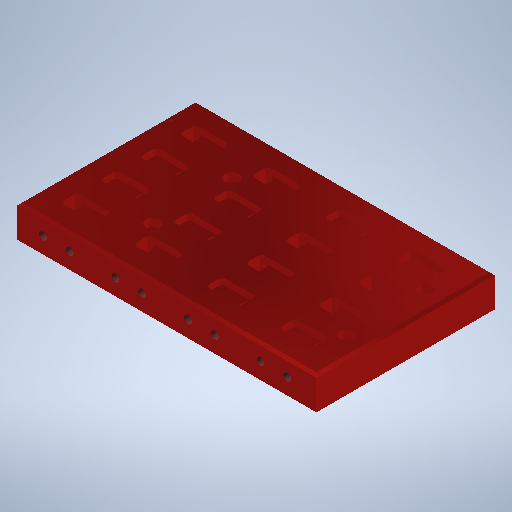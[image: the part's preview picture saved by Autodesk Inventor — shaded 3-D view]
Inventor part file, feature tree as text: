
AUTODESK INVENTOR PART (.ipt)
format: ipt  version: 2025 (Build 290162000, 162)  size: 1,054,208 bytes
history: native  units: mm
features: projected_geometry x17, sketch x9, hole x6, extrude x4, other x2, chamfer x1
ambient origin geometry x8: Origin, YZ Plane, XZ Plane, XY Plane, X Axis, Y Axis, Z Axis, Center Point
bodies: Volumenkörper1 (feature_tree)
feature tree (39):
  extrude  "Extrusion1"  Depth=140.0mm
  chamfer  "Fase1"  Distance=25.4mm
  hole  "Bohrung7"  [1 undecoded]
  extrude  "Extrusion6"  Depth=5.0mm
  hole  "Hole18"  [1 undecoded]
  extrude  "Extrusion10"  Depth=30.0mm
  sketch  "Sketch25"  dims[d169=3.0mm d170=6.0mm d171=8.0mm d172=4.6mm d173=14.3117mm d174=20.0mm d175=20.594885mm d259=27.0mm]
  hole  "Hole19"  [1 undecoded]
  extrude  "Extrusion11"  Depth=3.0mm
  hole  "Hole20"  [1 undecoded]
  sketch  "Sketch28"  dims[d267=40.0mm d269=57.0mm d270=40.0mm d272=31.0mm d277=5.0mm d278=0.0mm d382=76.2mm d383=152.4mm d384=31.0mm d385=62.0mm d386=6.528mm d387=6.0mm d388=11.113mm d389=6.35mm d390=14.3117mm d391=8.0mm d392=20.594885mm d476=17.0mm d477=17.0mm d478=17.0mm d479=20.0mm d480=0.75mm d481=0.75mm d482=0.75mm d483=0.75mm d484=1.5mm d485=1.5mm d486=1.5mm d487=1.5mm d488=3.0mm d489=3.75mm d490=5.25mm d491=3.75mm d492=5.25mm d493=40.0mm d495=57.0mm d496=40.0mm d498=31.0mm d501=1.2mm d502=0.0mm d503=50.0mm d504=25.4mm d505=12.7mm d506=21.0mm d507=20.0mm d508=40.0mm d510=57.0mm d511=10.0mm d513=10.0mm d515=5.9436mm d516=6.88594mm d517=0.624793mm d518=5.959094mm d519=11.0mm d520=2.6mm d521=90.0deg d522=28.0mm d523=20.594885mm d524=10.0mm d525=0.0mm d526=5.9436mm d527=6.886mm d528=0.624793mm d529=5.959094mm d530=4.0mm d531=2.0mm d532=90.0deg d533=59.0mm d534=20.594885mm d545=20.0mm d546=21.0mm d547=12.7mm d548=40.0mm d550=57.0mm d551=10.0mm d553=10.0mm d555=5.9436mm d556=6.886mm d557=0.624793mm d558=5.959094mm d559=4.0mm d560=2.0mm d561=90.0deg d562=59.0mm d563=20.594885mm d564=5.9436mm d565=6.88594mm d566=0.624793mm d567=5.959094mm d568=4.0mm d569=2.0mm d570=90.0deg d571=28.0mm d572=20.594885mm]
  hole  "Hole21"  [1 undecoded]
  hole  "Hole22"  [1 undecoded]
  sketch  "Skizze1"  dims[d0=235.0mm d2=140.0mm d3=25.4mm d4=0.0mm]
  other  "Alignment Holes"
  other  "Wells"
  sketch  "Sketch Rectangular Pattern1"  dims[d11=2.0mm d12=2.0mm d13=45.0deg d153=24.0mm]
  sketch  "Sketch24"  dims[d162=5.0mm]
  projected_geometry  "Projected Loop4"
  sketch  "Sketch Rectangular Pattern6"  dims[d154=24.0mm d155=5.0mm]
  sketch  "Sketch Rectangular Pattern7"  dims[d158=5.0mm d159=5.0mm]
  sketch  "Sketch26"  dims[d260=13.0mm d266=3.0mm]
  projected_geometry  "Projected Loop5"
  projected_geometry  "Projected Loop6"
  projected_geometry  "Projected Loop7"
  projected_geometry  "Projected Loop8"
  projected_geometry  "Projected Loop9"
  projected_geometry  "Projected Loop10"
  projected_geometry  "Projected Loop11"
  projected_geometry  "Projected Loop12"
  projected_geometry  "Projected Loop13"
  projected_geometry  "Projected Loop14"
  projected_geometry  "Projected Loop15"
  projected_geometry  "Projected Loop16"
  projected_geometry  "Projected Loop17"
  projected_geometry  "Projected Loop18"
  projected_geometry  "Projected Loop19"
  projected_geometry  "Projected Loop20"
  sketch  "Sketch Rectangular Pattern9"  dims[d160=30.0mm d161=30.0mm]
note: 6 required parameter values undecoded (feature->parameter linkage not recoverable at this tier; creation-order binding heuristic only, values carry confidence <= 0.55)
